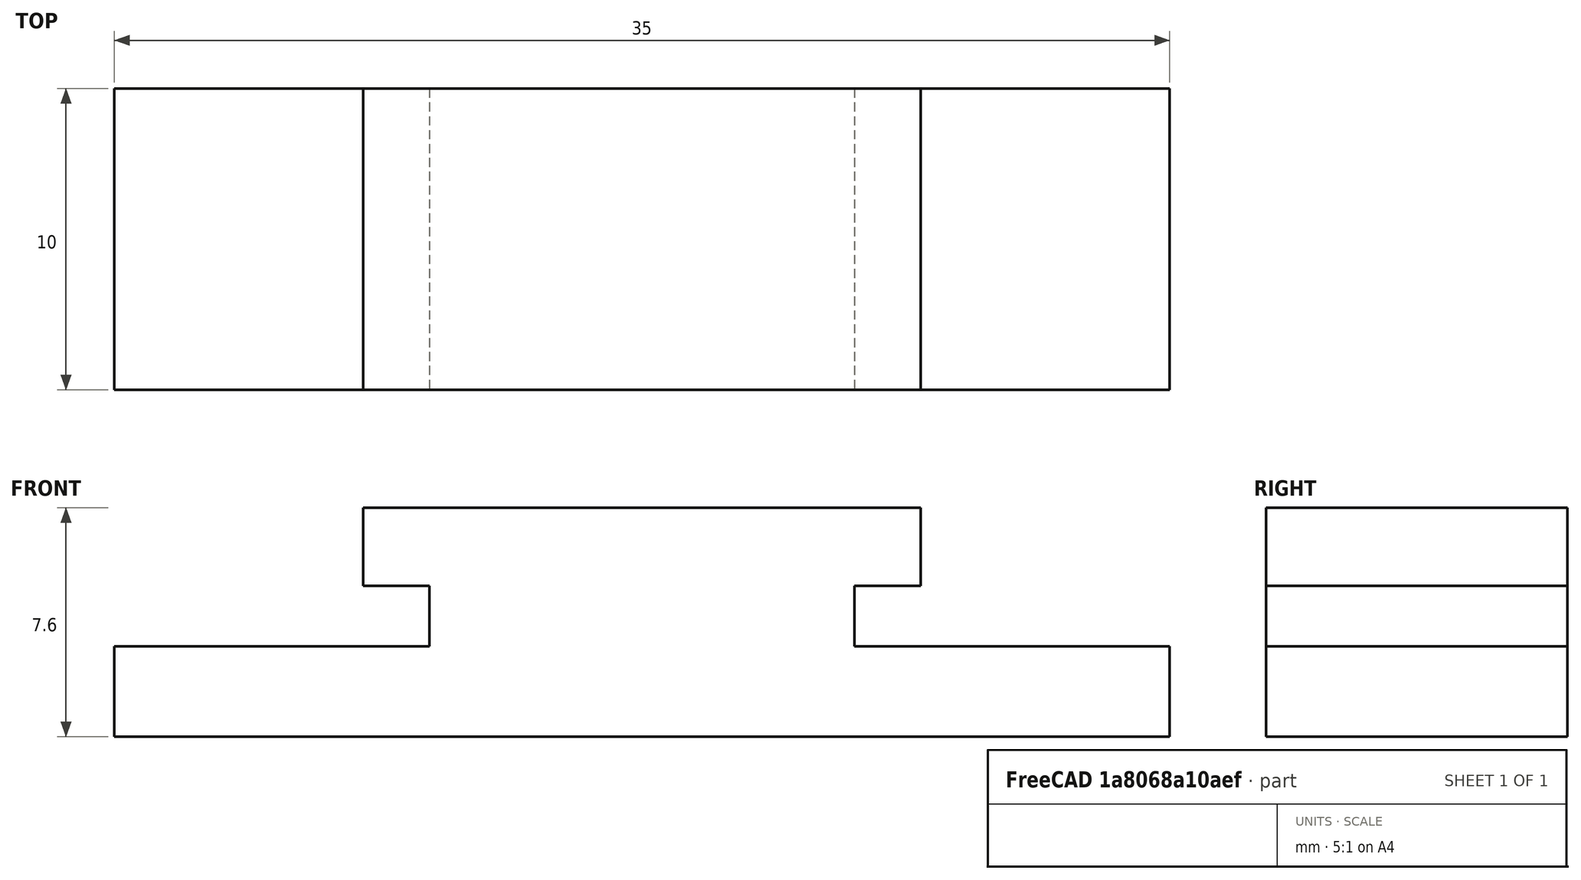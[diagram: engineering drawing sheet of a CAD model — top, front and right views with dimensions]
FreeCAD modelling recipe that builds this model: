
FCSTD DOCUMENT  (FreeCAD 0.19R23141 (Git))
Label: bike front light mount
License: All rights reserved
LicenseURL: http://en.wikipedia.org/wiki/All_rights_reserved
objects: Sketcher::SketchObject×1, PartDesign::Pad×1, PartDesign::Body×1
note: 4 computed .brp shape members not serialized (recipe doc carries the construction recipe); baked Part::Feature solids carry a one-line shape summary decoded from their .brp

FEATURE [Sketcher::SketchObject] Sketch
  MapMode = 5
  Placement = pos=(0,0,0) rot=(1,0,0;1.5708rad)
  Support = -> [XZ_Plane]
  sketch-geometry (12):
    g0: LineSegment StartX=9.25 StartY=7.6 StartZ=0 EndX=-9.25 EndY=7.6 EndZ=0
    g1: LineSegment StartX=-9.25 StartY=7.6 StartZ=0 EndX=-9.25 EndY=5 EndZ=0
    g2: LineSegment StartX=-9.25 StartY=5 StartZ=0 EndX=-7.05 EndY=5 EndZ=0
    g3: LineSegment StartX=-7.05 StartY=5 StartZ=0 EndX=-7.05 EndY=3 EndZ=0
    g4: LineSegment StartX=-7.05 StartY=3 StartZ=0 EndX=-17.5 EndY=3 EndZ=0
    g5: LineSegment StartX=-17.5 StartY=3 StartZ=0 EndX=-17.5 EndY=0 EndZ=0
    g6: LineSegment StartX=-17.5 StartY=0 StartZ=0 EndX=17.5 EndY=0 EndZ=0
    g7: LineSegment StartX=17.5 StartY=0 StartZ=0 EndX=17.5 EndY=3 EndZ=0
    g8: LineSegment StartX=17.5 StartY=3 StartZ=0 EndX=7.05 EndY=3 EndZ=0
    g9: LineSegment StartX=7.05 StartY=3 StartZ=0 EndX=7.05 EndY=5 EndZ=0
    g10: LineSegment StartX=7.05 StartY=5 StartZ=0 EndX=9.25 EndY=5 EndZ=0
    g11: LineSegment StartX=9.25 StartY=5 StartZ=0 EndX=9.25 EndY=7.6 EndZ=0
  constraints (32):
    c: Coincident(g11,g0)
    c: Coincident(g10,g11)
    c: Coincident(g9,g10)
    c: Coincident(g8,g9)
    c: Coincident(g7,g8)
    c: Coincident(g6,g7)
    c: Coincident(g6,g5)
    c: Coincident(g4,g5)
    c: Coincident(g3,g4)
    c: Coincident(g3,g2)
    c: Coincident(g2,g1)
    c: Coincident(g1,g0)
    c: Horizontal(g10)
    c: Horizontal(g8)
    c: Horizontal(g2)
    c: Horizontal(g4)
    c: Vertical(g5)
    c: Vertical(g1)
    c: Vertical(g11)
    c: Vertical(g9)
    c: Vertical(g7)
    c: Symmetric(g0,g0,g-2)
    c: Symmetric(g5,g6,g-2)
    c: Symmetric(g3,g8,g-2)
    c: Symmetric(g2,g9,g-2)
    c: DistanceX(g0,g0) = 18.5
    c: DistanceY(g1,g1) = 2.6
    c: DistanceX(g2,g2) = 2.2
    c: DistanceY(g3,g3) = 2
    c: DistanceY(g5,g5) = 3
    c: DistanceX(g6,g6) = 35
    c: PointOnObject(g-1,g6)
FEATURE [PartDesign::Pad] Pad
  Direction = (1,1,1)
  Length = 10
  Length2 = 100
  Placement = pos=(0,0,0) rot=(1,0,0;1.5708rad)
  Profile = -> Sketch
  Refine = true
  Type = 0
FEATURE [PartDesign::Body] Body
  Group = -> [Sketch,Pad]
  Origin = -> Origin
  Tip = -> Pad
